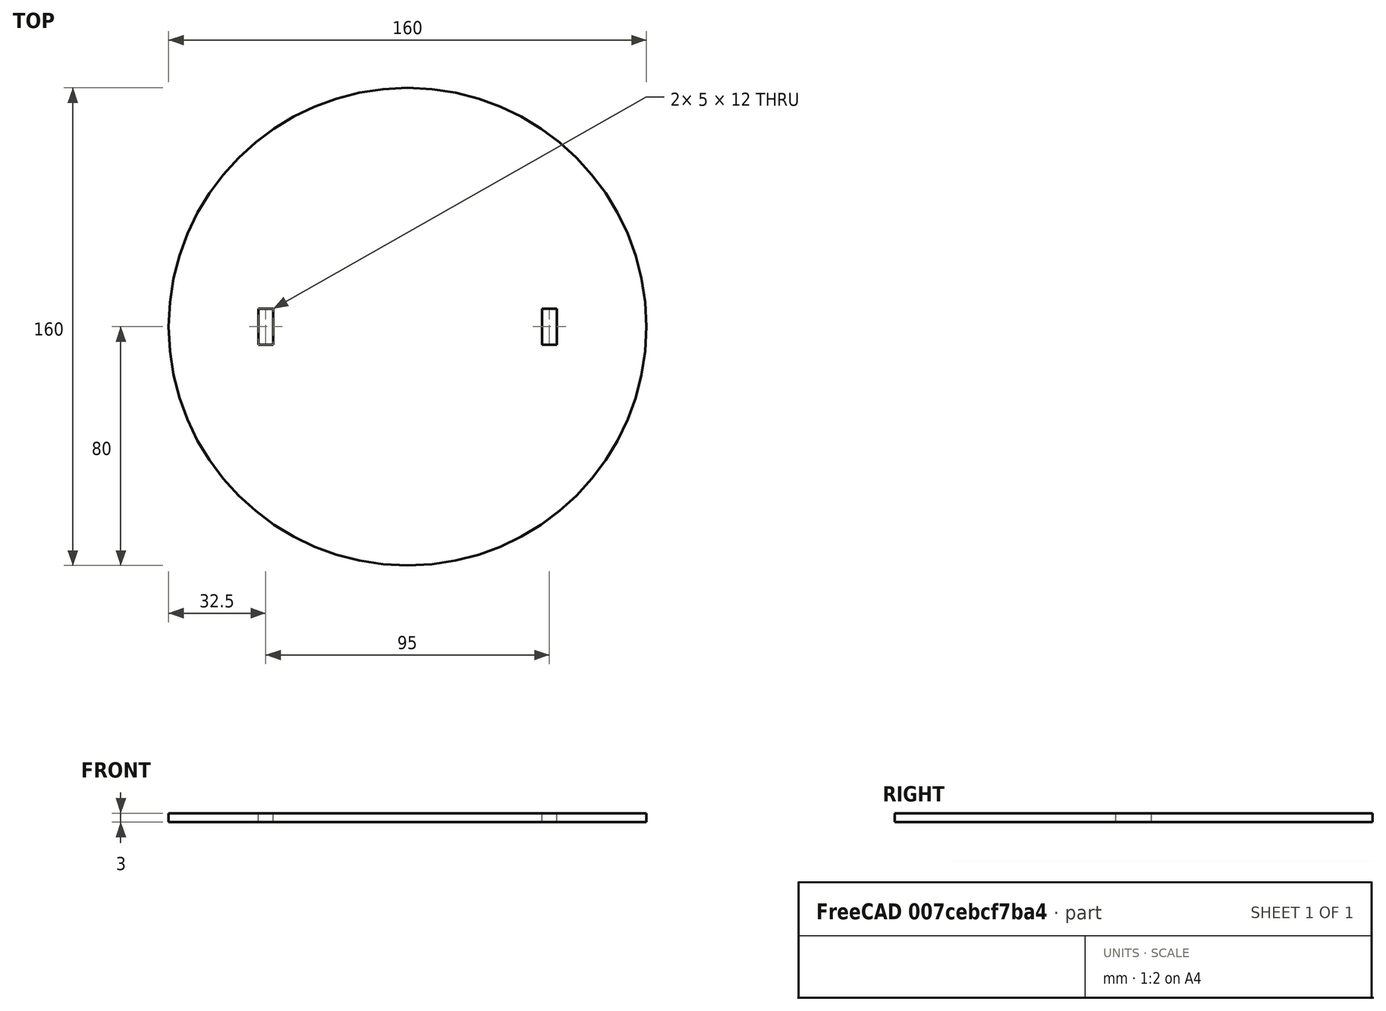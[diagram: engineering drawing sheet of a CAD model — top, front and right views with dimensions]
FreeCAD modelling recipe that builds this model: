
FCSTD DOCUMENT  (FreeCAD 0.17R13509 (Git))
Label: Hat
License: All rights reserved
LicenseURL: http://en.wikipedia.org/wiki/All_rights_reserved
objects: Sketcher::SketchObject×1, PartDesign::Pad×1, PartDesign::Body×1
note: 4 computed .brp shape members not serialized (recipe doc carries the construction recipe); baked Part::Feature solids carry a one-line shape summary decoded from their .brp

FEATURE [Sketcher::SketchObject] Sketch
  MapMode = 5
  Support = -> [XY_Plane]
  sketch-geometry (9):
    g0: Circle CenterX=0 CenterY=0 CenterZ=0 NormalX=0 NormalY=0 NormalZ=1 AngleXU=0 Radius=80
    g1: LineSegment StartX=-50 StartY=6 StartZ=0 EndX=-45 EndY=6 EndZ=0
    g2: LineSegment StartX=-45 StartY=6 StartZ=0 EndX=-45 EndY=-6 EndZ=0
    g3: LineSegment StartX=-45 StartY=-6 StartZ=0 EndX=-50 EndY=-6 EndZ=0
    g4: LineSegment StartX=-50 StartY=-6 StartZ=0 EndX=-50 EndY=6 EndZ=0
    g5: LineSegment StartX=45 StartY=6 StartZ=0 EndX=50 EndY=6 EndZ=0
    g6: LineSegment StartX=50 StartY=6 StartZ=0 EndX=50 EndY=-6 EndZ=0
    g7: LineSegment StartX=50 StartY=-6 StartZ=0 EndX=45 EndY=-6 EndZ=0
    g8: LineSegment StartX=45 StartY=-6 StartZ=0 EndX=45 EndY=6 EndZ=0
  constraints (26):
    c: Coincident(g0,g-1)
    c: Radius(g0) = 80
    c: Coincident(g1,g2)
    c: Coincident(g2,g3)
    c: Coincident(g3,g4)
    c: Coincident(g4,g1)
    c: Horizontal(g1)
    c: Horizontal(g3)
    c: Vertical(g2)
    c: Vertical(g4)
    c: Coincident(g5,g6)
    c: Coincident(g6,g7)
    c: Coincident(g7,g8)
    c: Coincident(g8,g5)
    c: Horizontal(g5)
    c: Horizontal(g7)
    c: Vertical(g6)
    c: Vertical(g8)
    c: Equal(g3,g7)
    c: Equal(g4,g8)
    c: Symmetric(g1,g5,g-2)
    c: Symmetric(g5,g1,g-2)
    c: Symmetric(g6,g5,g-1)
    c: DistanceX(g1,g1) = 5
    c: DistanceY(g4,g4) = 12
    c: DistanceX(g1,g5) = 100
FEATURE [PartDesign::Pad] Pad
  Length = 3
  Length2 = 100
  Profile = -> Sketch
  Refine = true
  Type = 0
FEATURE [PartDesign::Body] Body
  Group = -> [Sketch,Pad]
  Origin = -> Origin
  Tip = -> Pad
